# Revit family: LF4SQSL
name_source: partatom
category: Lighting Fixtures
revit_build: Autodesk Revit 2014 (Build: 20130308_1515(x64)
units: mm (PartAtom-declared; Revit-internal decimal feet)

## types (1)
- LF4SQ
    Apparent Load = 14 VA
    Application = Commerical Indoor
Education
Healthcare
Hospitality
Office
Lobby
Conference Room
Classroom
Waiting Room
Auditorium
Guest Room
Dining Area
    Color Filter = 16777215
    Default Elevation = 48"
    Description = 4" LED Square Downlight
    Dimming Lamp Color Temperature Shift = <None>
    Dimming Protocol = 0-10V
DMX
Lutron Forward Phase
Lutron EcoSystem
    Emit Shape Visible in Rendering = No
    Emit from Rectangle Length = 4 3/16"
    Emit from Rectangle Width = 4 3/16"
    Glass = Glass
    Height = 6 5/8"
    Lamp = 1
    Length = 14"
    Load Classification = Lighting
    Manufacturer = Healthcare Solutions
    Model = LF4SQSL
    Number of Poles = 1
    Photometric Web File = generic.ies
    Power Factor = 0.9
    Product Documentation Link = https://hubbellcdn.com
    Product Material = Steel
    Product Page URL = https://www.hubbell.com
    SQ Length = 2 7/8"
    Tilt Angle = -90.00°
    URL = https://www.hubbell.com
    Voltage = 120 V
    Wattage Comments = 14W
    Width = 12 5/8"

## geometry (parser evidence)
native form markers: Blend x1, Sweep x2
no freeform markers — native parametric forms only
